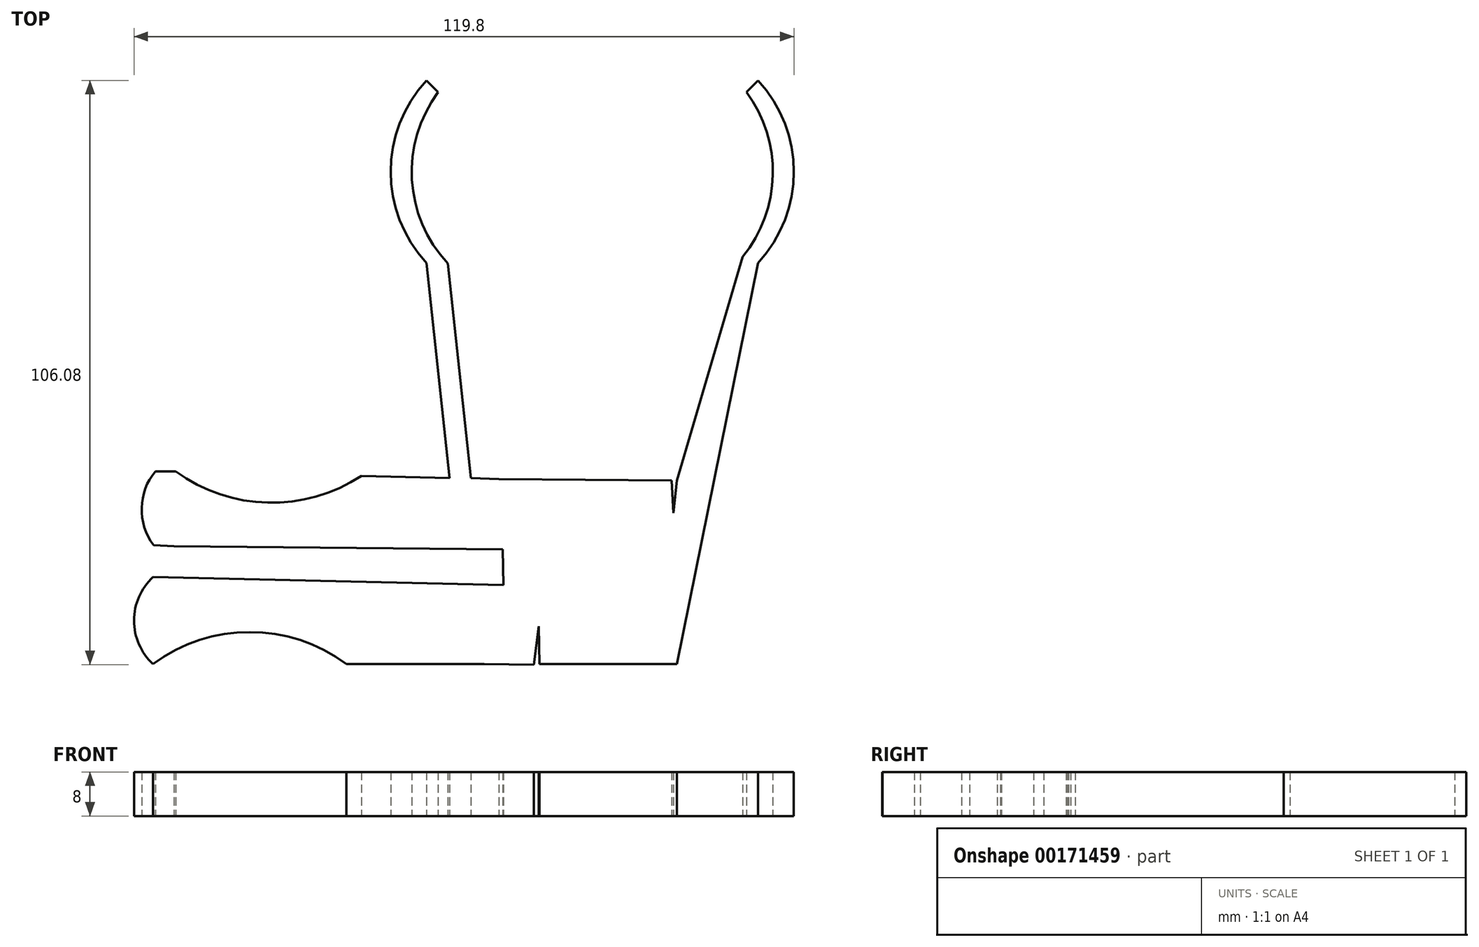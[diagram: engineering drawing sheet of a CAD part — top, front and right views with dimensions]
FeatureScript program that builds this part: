
annotation { "Feature Type Name" : "Feature", "Feature Type Description" : "" }
export const myFeature = defineFeature(function(context is Context, id is Id, definition is map)
    precondition{}
    {
        {
            var Q0;
            Q0=qCreatedBy(makeId("Top.planeOp"),FACE);
            var sketch = newSketch(context, id + "F0", { "sketchPlane" : qUnion([Q0])});
            skLineSegment(sketch, "E0", {"start": v(-34.88, -37.95) * mm, "end": v(-9.88, -37.95) * mm});
            skLineSegment(sketch, "E1", {"start": v(0.12, -37.95) * mm, "end": v(25.12, -37.95) * mm});
            skArc(sketch, "E2", {"start": v(-34.88, -37.95) * mm, "mid": v(-52.46, -32.13) * mm, "end": v(-70.03, -37.95) * mm});
            skArc(sketch, "E3", {"start": v(-70.03, -22.13) * mm, "mid": v(-73.46, -30.04) * mm, "end": v(-70.03, -37.95) * mm});
            skLineSegment(sketch, "E4", {"start": v(-70.03, -22.13) * mm, "end": v(-6.4, -23.59) * mm});
            skArc(sketch, "E5.MirrorCS", {"start": v(-69.93, -16.32) * mm, "mid": v(-72.08, -9.57) * mm, "end": v(-69.6, -2.93) * mm});
            skArc(sketch, "E6.MirrorCS", {"start": v(-32.2, -3.74) * mm, "mid": v(-49.17, -8.63) * mm, "end": v(-65.87, -2.93) * mm});
            skLineSegment(sketch, "E7", {"start": v(-16.17, -4.15) * mm, "end": v(-20.36, 34.92) * mm});
            skArc(sketch, "E8", {"start": v(-20.36, 68.05) * mm, "mid": v(-26.86, 51.49) * mm, "end": v(-20.36, 34.92) * mm});
            skLineSegment(sketch, "E9", {"start": v(-20.36, 68.05) * mm, "end": v(-18.24, 65.93) * mm});
            skArc(sketch, "E10", {"start": v(-18.24, 65.93) * mm, "mid": v(-23, 50.05) * mm, "end": v(-16.5, 34.81) * mm});
            skLineSegment(sketch, "E11", {"start": v(-16.5, 34.81) * mm, "end": v(-12.32, -4.15) * mm});
            skArc(sketch, "E12.MirrorCS", {"start": v(37.71, 65.93) * mm, "mid": v(42.51, 50.88) * mm, "end": v(37.05, 36.06) * mm});
            skArc(sketch, "E13.MirrorCS", {"start": v(39.83, 68.05) * mm, "mid": v(46.34, 51.49) * mm, "end": v(39.83, 34.92) * mm});
            skLineSegment(sketch, "E14", {"start": v(39.83, 68.05) * mm, "end": v(37.71, 65.93) * mm});
            skLineSegment(sketch, "E15", {"start": v(39.83, 34.92) * mm, "end": v(25.12, -37.95) * mm});
            skLineSegment(sketch, "E16", {"start": v(37.05, 36.06) * mm, "end": v(25.12, -4.6) * mm});
            skLineSegment(sketch, "E17", {"start": v(-6.4, -23.59) * mm, "end": v(-6.5, -17.08) * mm});
            skLineSegment(sketch, "E18", {"start": v(-32.2, -3.74) * mm, "end": v(-16.17, -4.15) * mm});
            skLineSegment(sketch, "E19", {"start": v(-12.32, -4.15) * mm, "end": v(-7.22, -4.34) * mm});
            skLineSegment(sketch, "E20", {"start": v(-7.22, -4.34) * mm, "end": v(24.12, -4.6) * mm});
            skLineSegment(sketch, "E21", {"start": v(25.12, -4.6) * mm, "end": v(24.47, -10.53) * mm});
            skLineSegment(sketch, "E22", {"start": v(24.12, -4.6) * mm, "end": v(24.47, -10.53) * mm});
            skLineSegment(sketch, "E23", {"start": v(-9.88, -37.95) * mm, "end": v(-0.88, -38.03) * mm});
            skLineSegment(sketch, "E24", {"start": v(-0.88, -38.03) * mm, "end": v(0, -31.1) * mm});
            skLineSegment(sketch, "E25", {"start": v(0.12, -37.95) * mm, "end": v(0, -31.1) * mm});
            skLineSegment(sketch, "E26", {"start": v(-69.6, -2.93) * mm, "end": v(-65.87, -2.93) * mm});
            skLineSegment(sketch, "E27", {"start": v(-69.93, -16.32) * mm, "end": v(-66.21, -16.55) * mm});
            skLineSegment(sketch, "E28", {"start": v(-66.21, -16.55) * mm, "end": v(-53.5, -16.66) * mm});
            skLineSegment(sketch, "E29", {"start": v(-39.31, -16.79) * mm, "end": v(-53.5, -16.66) * mm});
            skLineSegment(sketch, "E30", {"start": v(-39.31, -16.79) * mm, "end": v(-23.01, -16.93) * mm});
            skLineSegment(sketch, "E31", {"start": v(-23.01, -16.93) * mm, "end": v(-6.5, -17.08) * mm});
            skSolve(sketch);
        }
        {
            var Q0;
            Q0=makeQuery(id+"F0.imprint","IMPRINT",FACE,{"disambiguationData":[TD([[makeQuery(id+"F0.imprint","IMPRINT",EDGE,{"derivedFrom":sQuery(id+"F0.wireOp",EDGE,"E0")}),1.0]])]});
            extrude(context, id + "F1", {"entities" : qUnion([Q0]), "depth" : 8 * mm});
        }
    });
